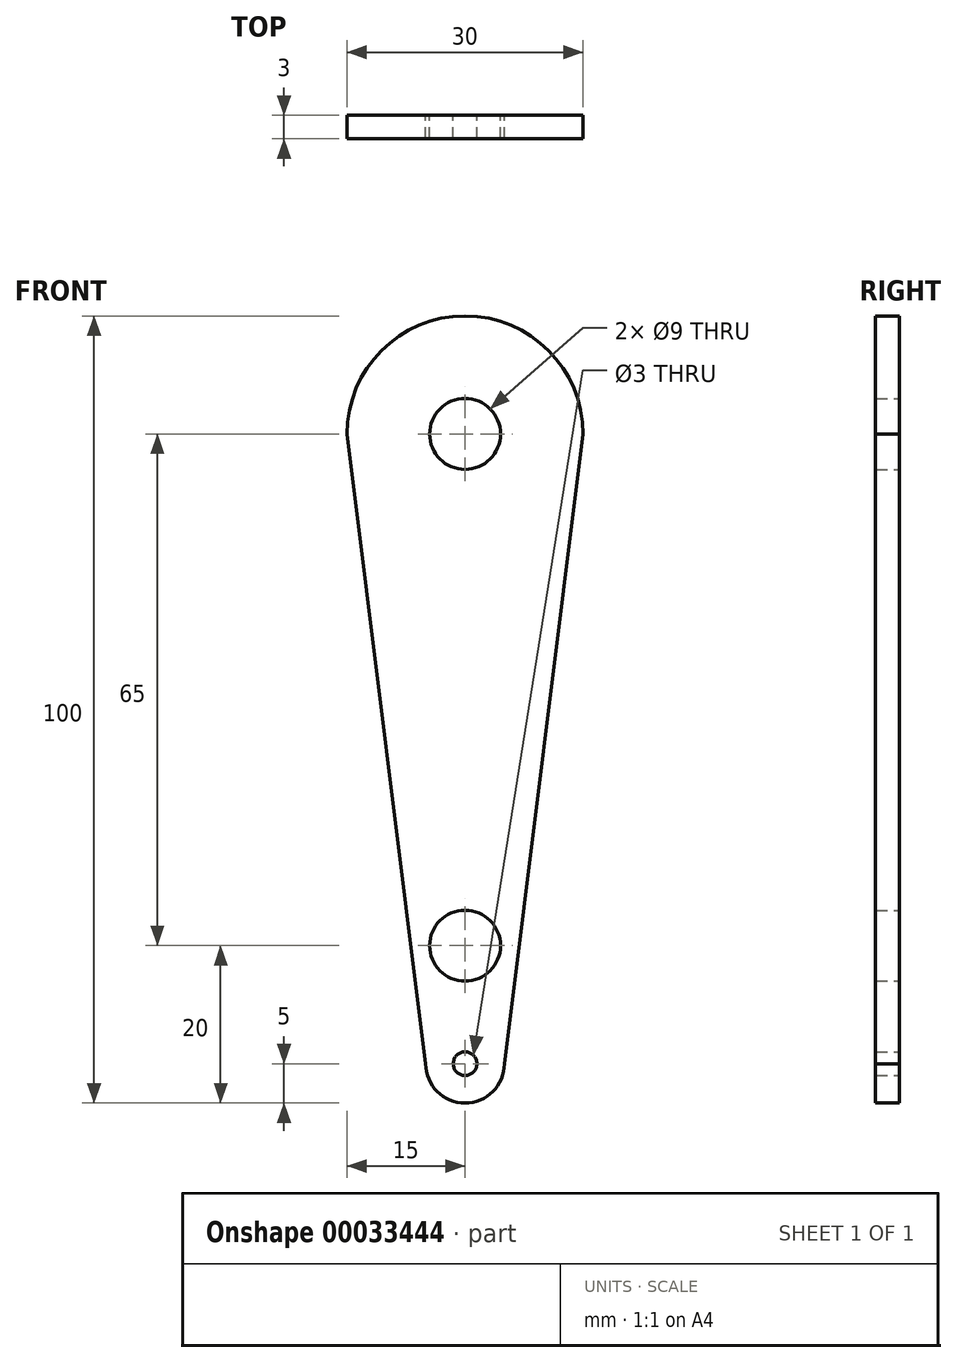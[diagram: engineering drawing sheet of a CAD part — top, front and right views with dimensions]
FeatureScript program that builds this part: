
annotation { "Feature Type Name" : "Feature", "Feature Type Description" : "" }
export const myFeature = defineFeature(function(context is Context, id is Id, definition is map)
    precondition{}
    {
        {
            var Q0;
            Q0=qCreatedBy(makeId("Front.planeOp"),FACE);
            var sketch = newSketch(context, id + "F0", { "sketchPlane" : qUnion([Q0])});
            skLineSegment(sketch, "E0.rect.bottom", {"start": v(-15, -50) * mm, "end": v(15, -50) * mm});
            skLineSegment(sketch, "E0.rect.top", {"start": v(-15, 50) * mm, "end": v(15, 50) * mm});
            skLineSegment(sketch, "E0.rect.left", {"start": v(-15, -50) * mm, "end": v(-15, 50) * mm});
            skLineSegment(sketch, "E0.rect.right", {"start": v(15, -50) * mm, "end": v(15, 50) * mm});
            skPoint(sketch, "E0.rect.middle", {"position": v(0, 0) * mm});
            skLineSegment(sketch, "E1.0", {"start": v(-15, 35) * mm, "end": v(15, 35) * mm, "construction": true});
            skLineSegment(sketch, "E2.0", {"start": v(0, -50) * mm, "end": v(0, 50) * mm, "construction": true});
            skLineSegment(sketch, "E3.0", {"start": v(-15, -30) * mm, "end": v(15, -30) * mm, "construction": true});
            skLineSegment(sketch, "E4.0", {"start": v(-15, -37) * mm, "end": v(15, -37) * mm, "construction": true});
            skLineSegment(sketch, "E5.0", {"start": v(-15, -45) * mm, "end": v(15, -45) * mm, "construction": true});
            skArc(sketch, "E6", {"start": v(15, 35) * mm, "mid": v(0, 50) * mm, "end": v(-15, 35) * mm});
            skLineSegment(sketch, "E7.0", {"start": v(5, -50) * mm, "end": v(5, 50) * mm, "construction": true});
            skLineSegment(sketch, "E8.0", {"start": v(-5, -50) * mm, "end": v(-5, 50) * mm, "construction": true});
            skArc(sketch, "E9", {"start": v(-5, -45) * mm, "mid": v(0, -50) * mm, "end": v(5, -45) * mm});
            skLineSegment(sketch, "E10", {"start": v(-15, 35) * mm, "end": v(-5, -45) * mm});
            skLineSegment(sketch, "E11", {"start": v(15, 35) * mm, "end": v(5, -45) * mm});
            skCircle(sketch, "E12", {"center": v(0, 35) * mm, "radius": 4.5 * mm});
            skCircle(sketch, "E13", {"center": v(0, -45) * mm, "radius": 1.5 * mm});
            skCircle(sketch, "E14", {"center": v(0, -30) * mm, "radius": 4.5 * mm});
            skSolve(sketch);
        }
        {
            var Q0;
            {var subQ1=sQuery(id+"F0.wireOp",EDGE,"E10");Q0=makeQuery(id+"F0.imprint","IMPRINT",FACE,{"disambiguationData":[TD([[makeQuery(id+"F0.imprint","IMPRINT",EDGE,{"derivedFrom":subQ1}),1.0]])]});}
            extrude(context, id + "F1", {"entities" : qUnion([Q0]), "depth" : 3 * mm});
        }
    });
